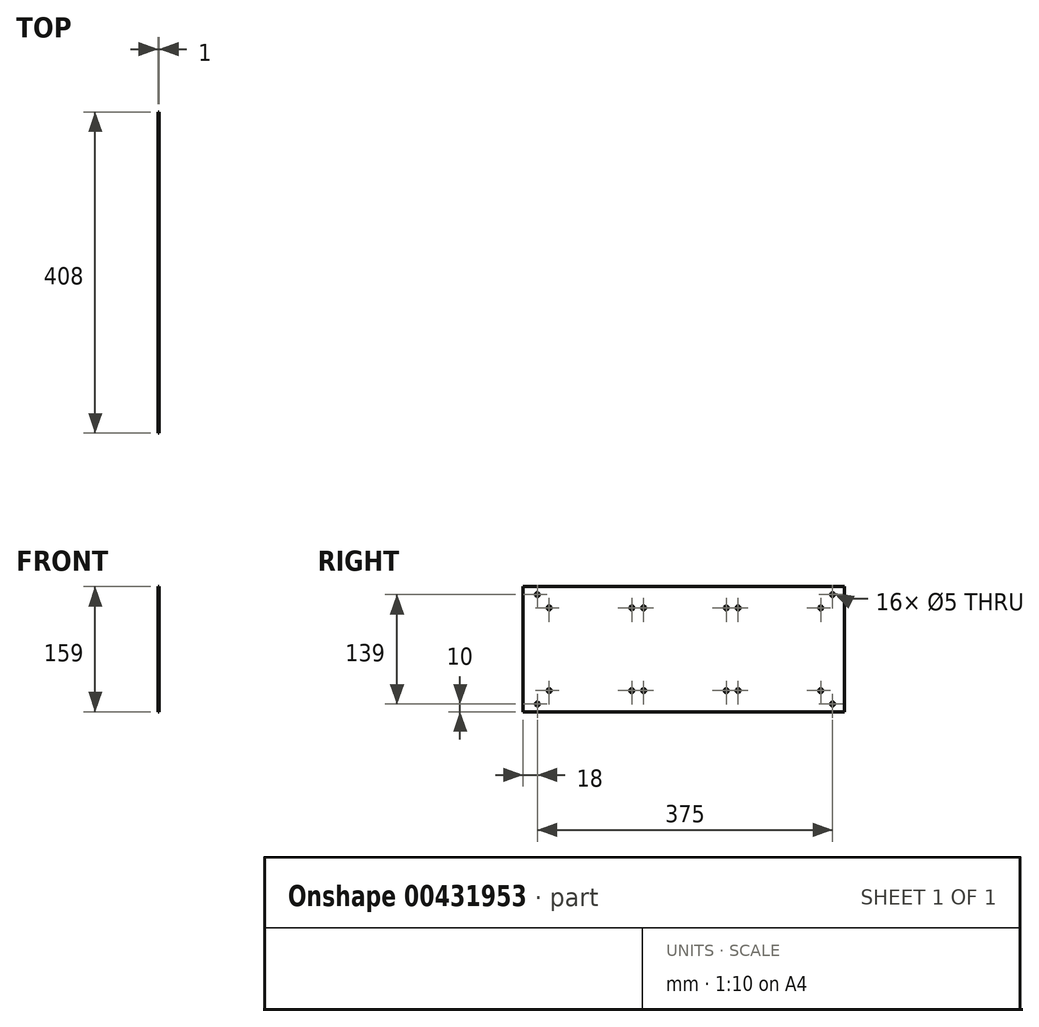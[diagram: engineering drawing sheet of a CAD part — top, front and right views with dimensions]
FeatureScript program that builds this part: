
annotation { "Feature Type Name" : "Feature", "Feature Type Description" : "" }
export const myFeature = defineFeature(function(context is Context, id is Id, definition is map)
    precondition{}
    {
        {
            var Q0;
            Q0=qCreatedBy(makeId("Right.planeOp"),FACE);
            var sketch = newSketch(context, id + "F0", { "sketchPlane" : qUnion([Q0])});
            skLineSegment(sketch, "E0.bottom", {"start": v(-207.5, 84.5) * mm, "end": v(207.5, 84.5) * mm});
            skLineSegment(sketch, "E0.top", {"start": v(-207.5, -84.5) * mm, "end": v(207.5, -84.5) * mm});
            skLineSegment(sketch, "E0.left", {"start": v(-207.5, 84.5) * mm, "end": v(-207.5, -84.5) * mm});
            skLineSegment(sketch, "E0.right", {"start": v(207.5, 84.5) * mm, "end": v(207.5, -84.5) * mm});
            skPoint(sketch, "E0.middle", {"position": v(0, 0) * mm});
            skSolve(sketch);
        }
        {
            var Q0;
            Q0=qSketchRegion(id+"F0",true);
            extrude(context, id + "F1", {"entities" : qUnion([Q0]), "depth" : 24 * mm});
        }
        {
            var Q0;
            Q0=makeQuery(id+"F1.opExtrude","CAP_FACE",FACE,{"disambiguationData":[OSD([sQuery(id+"F0.wireOp",EDGE,"E0.bottom"),sQuery(id+"F0.wireOp",EDGE,"E0.top"),sQuery(id+"F0.wireOp",EDGE,"E0.left"),sQuery(id+"F0.wireOp",EDGE,"E0.right")])],"isStart":false});
            var sketch = newSketch(context, id + "F2", { "sketchPlane" : qUnion([Q0])});
            skLineSegment(sketch, "E1.bottom", {"start": v(-206.5, 83.5) * mm, "end": v(206.5, 83.5) * mm});
            skLineSegment(sketch, "E1.top", {"start": v(-206.5, -83.5) * mm, "end": v(206.5, -83.5) * mm});
            skLineSegment(sketch, "E1.left", {"start": v(-206.5, 83.5) * mm, "end": v(-206.5, -83.5) * mm});
            skLineSegment(sketch, "E1.right", {"start": v(206.5, 83.5) * mm, "end": v(206.5, -83.5) * mm});
            skPoint(sketch, "E1.middle", {"position": v(0, 0) * mm});
            skSolve(sketch);
        }
        {
            var Q0;
            Q0=qSketchRegion(id+"F2",true);
            extrude(context, id + "F3", {"entities" : qUnion([Q0]), "operationType" : NewBodyOperationType.REMOVE, "oppositeDirection" : true, "depth" : 23 * mm});
        }
        {
            var Q0;
            Q0=makeQuery(id+"F1.opExtrude","SWEPT_FACE",FACE,{"disambiguationData":[OSD([sQuery(id+"F0.wireOp",EDGE,"E0.left")])]});
            var sketch = newSketch(context, id + "F4", { "sketchPlane" : qUnion([Q0])});
            skLineSegment(sketch, "E2", {"start": v(24, -83.5) * mm, "end": v(8, -83.5) * mm});
            skLineSegment(sketch, "E3", {"start": v(8, -83.5) * mm, "end": v(8, -64.5) * mm});
            skLineSegment(sketch, "E4", {"start": v(18, -76.5) * mm, "end": v(18, -64.5) * mm});
            skLineSegment(sketch, "E5", {"start": v(18, -64.5) * mm, "end": v(8, -64.5) * mm, "construction": true});
            skArc(sketch, "E6", {"start": v(8, -64.5) * mm, "mid": v(13, -59.5) * mm, "end": v(18, -64.5) * mm});
            skLineSegment(sketch, "E7", {"start": v(18, -76.5) * mm, "end": v(19.5, -77.5) * mm});
            skLineSegment(sketch, "E8", {"start": v(24, -75.5) * mm, "end": v(24, -83.5) * mm});
            skLineSegment(sketch, "E9", {"start": v(19.5, -77.5) * mm, "end": v(24, -75.5) * mm});
            skLineSegment(sketch, "E10", {"start": v(0, 0) * mm, "end": v(24, 0) * mm, "construction": true});
            skLineSegment(sketch, "E11.MirrorCS", {"start": v(18, 76.5) * mm, "end": v(19.5, 77.5) * mm});
            skLineSegment(sketch, "E12.MirrorCS", {"start": v(24, 75.5) * mm, "end": v(24, 83.5) * mm});
            skLineSegment(sketch, "E13.MirrorCS", {"start": v(19.5, 77.5) * mm, "end": v(24, 75.5) * mm});
            skLineSegment(sketch, "E14.MirrorCS", {"start": v(18, 64.5) * mm, "end": v(8, 64.5) * mm, "construction": true});
            skLineSegment(sketch, "E15.MirrorCS", {"start": v(18, 76.5) * mm, "end": v(18, 64.5) * mm});
            skArc(sketch, "E16.MirrorCS", {"start": v(8, 64.5) * mm, "mid": v(13, 59.5) * mm, "end": v(18, 64.5) * mm});
            skLineSegment(sketch, "E17.MirrorCS", {"start": v(24, 83.5) * mm, "end": v(8, 83.5) * mm});
            skLineSegment(sketch, "E18.MirrorCS", {"start": v(8, 83.5) * mm, "end": v(8, 64.5) * mm});
            skSolve(sketch);
        }
        {
            var Q0;
            Q0=qSketchRegion(id+"F4",true);
            extrude(context, id + "F5", {"entities" : qUnion([Q0]), "operationType" : NewBodyOperationType.REMOVE, "endBound" : BoundingType.THROUGH_ALL, "oppositeDirection" : true, "depth" : 25 * mm});
        }
        {
            var Q0;
            Q0=makeQuery(id+"F1.opExtrude","SWEPT_FACE",FACE,{"disambiguationData":[OSD([sQuery(id+"F0.wireOp",EDGE,"E0.left")])]});
            var sketch = newSketch(context, id + "F6", { "sketchPlane" : qUnion([Q0])});
            skCircle(sketch, "E19", {"center": v(12.5, 50.5) * mm, "radius": 1.5 * mm});
            skSolve(sketch);
        }
        {
            var Q0;
            Q0=qSketchRegion(id+"F6",true);
            extrude(context, id + "F7", {"entities" : qUnion([Q0]), "operationType" : NewBodyOperationType.REMOVE, "endBound" : BoundingType.THROUGH_ALL, "oppositeDirection" : true, "depth" : 25 * mm});
        }
        {
            var Q0;
            Q0=makeQuery(id+"F1.opExtrude","CAP_FACE",FACE,{"disambiguationData":[OSD([sQuery(id+"F0.wireOp",EDGE,"E0.bottom"),sQuery(id+"F0.wireOp",EDGE,"E0.top"),sQuery(id+"F0.wireOp",EDGE,"E0.left"),sQuery(id+"F0.wireOp",EDGE,"E0.right")])],"isStart":true});
            var sketch = newSketch(context, id + "F8", { "sketchPlane" : qUnion([Q0])});
            skCircle(sketch, "E20", {"center": v(-172.5, 52.5) * mm, "radius": 2.5 * mm});
            skCircle(sketch, "E21", {"center": v(-67.5, 52.5) * mm, "radius": 2.5 * mm});
            skCircle(sketch, "E22", {"center": v(-52.5, 52.5) * mm, "radius": 2.5 * mm});
            skLineSegment(sketch, "E23", {"start": v(0, 0) * mm, "end": v(-207.5, 0) * mm, "construction": true});
            skCircle(sketch, "E24.MirrorC", {"center": v(-67.5, -52.5) * mm, "radius": 2.5 * mm});
            skCircle(sketch, "E25.MirrorC", {"center": v(-172.5, -52.5) * mm, "radius": 2.5 * mm});
            skCircle(sketch, "E26.MirrorC", {"center": v(-52.5, -52.5) * mm, "radius": 2.5 * mm});
            skLineSegment(sketch, "E27", {"start": v(0, 84.5) * mm, "end": v(0, -84.5) * mm, "construction": true});
            skCircle(sketch, "E28.MirrorC", {"center": v(67.5, -52.5) * mm, "radius": 2.5 * mm});
            skCircle(sketch, "E29.MirrorC", {"center": v(52.5, 52.5) * mm, "radius": 2.5 * mm});
            skCircle(sketch, "E30.MirrorC", {"center": v(67.5, 52.5) * mm, "radius": 2.5 * mm});
            skCircle(sketch, "E31.MirrorC", {"center": v(172.5, 52.5) * mm, "radius": 2.5 * mm});
            skCircle(sketch, "E32.MirrorC", {"center": v(172.5, -52.5) * mm, "radius": 2.5 * mm});
            skCircle(sketch, "E33.MirrorC", {"center": v(52.5, -52.5) * mm, "radius": 2.5 * mm});
            skSolve(sketch);
        }
        {
            var Q0;
            Q0=qSketchRegion(id+"F8",true);
            extrude(context, id + "F9", {"entities" : qUnion([Q0]), "operationType" : NewBodyOperationType.REMOVE, "endBound" : BoundingType.UP_TO_NEXT, "oppositeDirection" : true, "depth" : 25 * mm});
        }
        {
            var Q0;
            Q0=makeQuery(id+"F1.opExtrude","CAP_FACE",FACE,{"disambiguationData":[OSD([sQuery(id+"F0.wireOp",EDGE,"E0.bottom"),sQuery(id+"F0.wireOp",EDGE,"E0.top"),sQuery(id+"F0.wireOp",EDGE,"E0.left"),sQuery(id+"F0.wireOp",EDGE,"E0.right")])],"isStart":true});
            var sketch = newSketch(context, id + "F10", { "sketchPlane" : qUnion([Q0])});
            skLineSegment(sketch, "E34.bottom", {"start": v(-207.5, 84.5) * mm, "end": v(207.5, 84.5) * mm});
            skLineSegment(sketch, "E34.top", {"start": v(-202.5, 79.5) * mm, "end": v(205.5, 79.5) * mm});
            skLineSegment(sketch, "E34.left", {"start": v(-207.5, 84.5) * mm, "end": v(-207.5, 79.5) * mm});
            skLineSegment(sketch, "E34.right", {"start": v(207.5, 84.5) * mm, "end": v(207.5, 79.5) * mm});
            skLineSegment(sketch, "E35.bottom", {"start": v(-207.5, -84.5) * mm, "end": v(207.5, -84.5) * mm});
            skLineSegment(sketch, "E35.top", {"start": v(-202.5, -79.5) * mm, "end": v(205.5, -79.5) * mm});
            skLineSegment(sketch, "E35.left", {"start": v(-207.5, -84.5) * mm, "end": v(-207.5, -79.5) * mm});
            skLineSegment(sketch, "E35.right", {"start": v(207.5, -84.5) * mm, "end": v(207.5, -79.5) * mm});
            skLineSegment(sketch, "E36.left", {"start": v(207.5, 79.5) * mm, "end": v(207.5, -79.5) * mm});
            skLineSegment(sketch, "E36.right", {"start": v(205.5, 79.5) * mm, "end": v(205.5, -79.5) * mm});
            skLineSegment(sketch, "E37.left", {"start": v(-207.5, 79.5) * mm, "end": v(-207.5, -79.5) * mm});
            skLineSegment(sketch, "E37.right", {"start": v(-202.5, 79.5) * mm, "end": v(-202.5, -79.5) * mm});
            skSolve(sketch);
        }
        {
            var Q0;
            Q0=makeQuery(id+"F10.imprint","IMPRINT",FACE,{"disambiguationData":[TD([[makeQuery(id+"F10.imprint","IMPRINT",EDGE,{"derivedFrom":sQuery(id+"F10.wireOp",EDGE,"E34.bottom")}),1.0]])]});
            extrude(context, id + "F11", {"entities" : qUnion([Q0]), "operationType" : NewBodyOperationType.REMOVE, "endBound" : BoundingType.UP_TO_NEXT, "oppositeDirection" : true, "depth" : 25 * mm});
        }
        {
            var Q0;
            Q0=makeQuery(id+"F1.opExtrude","CAP_FACE",FACE,{"disambiguationData":[OSD([sQuery(id+"F0.wireOp",EDGE,"E0.bottom"),sQuery(id+"F0.wireOp",EDGE,"E0.top"),sQuery(id+"F0.wireOp",EDGE,"E0.left"),sQuery(id+"F0.wireOp",EDGE,"E0.right")])],"isStart":true});
            var sketch = newSketch(context, id + "F12", { "sketchPlane" : qUnion([Q0])});
            skCircle(sketch, "E38", {"center": v(-187.5, 69.5) * mm, "radius": 2.5 * mm});
            skLineSegment(sketch, "E39", {"start": v(-206.53, 0) * mm, "end": v(205.5, 0) * mm, "construction": true});
            skPoint(sketch, "E39.startSnap0", {"position": v(-202.5, 0) * mm});
            skCircle(sketch, "E40.MirrorC", {"center": v(-187.5, -69.5) * mm, "radius": 2.5 * mm});
            skPoint(sketch, "E41.MirrorP", {"position": v(205.5, 0) * mm});
            skLineSegment(sketch, "E42", {"start": v(0, 79.5) * mm, "end": v(0, -79.5) * mm, "construction": true});
            skCircle(sketch, "E43.MirrorC", {"center": v(187.5, 69.5) * mm, "radius": 2.5 * mm});
            skCircle(sketch, "E44.MirrorC", {"center": v(187.5, -69.5) * mm, "radius": 2.5 * mm});
            skPoint(sketch, "E45.MirrorP", {"position": v(202.5, 0) * mm});
            skSolve(sketch);
        }
        {
            var Q0;
            Q0 = qSketchRegion(id + "F12", true);
            extrude(context, id + "F13", {"entities" : qUnion([Q0]), "operationType" : NewBodyOperationType.REMOVE, "endBound" : BoundingType.UP_TO_NEXT, "oppositeDirection" : true, "depth" : 25 * mm});
        }
    });
